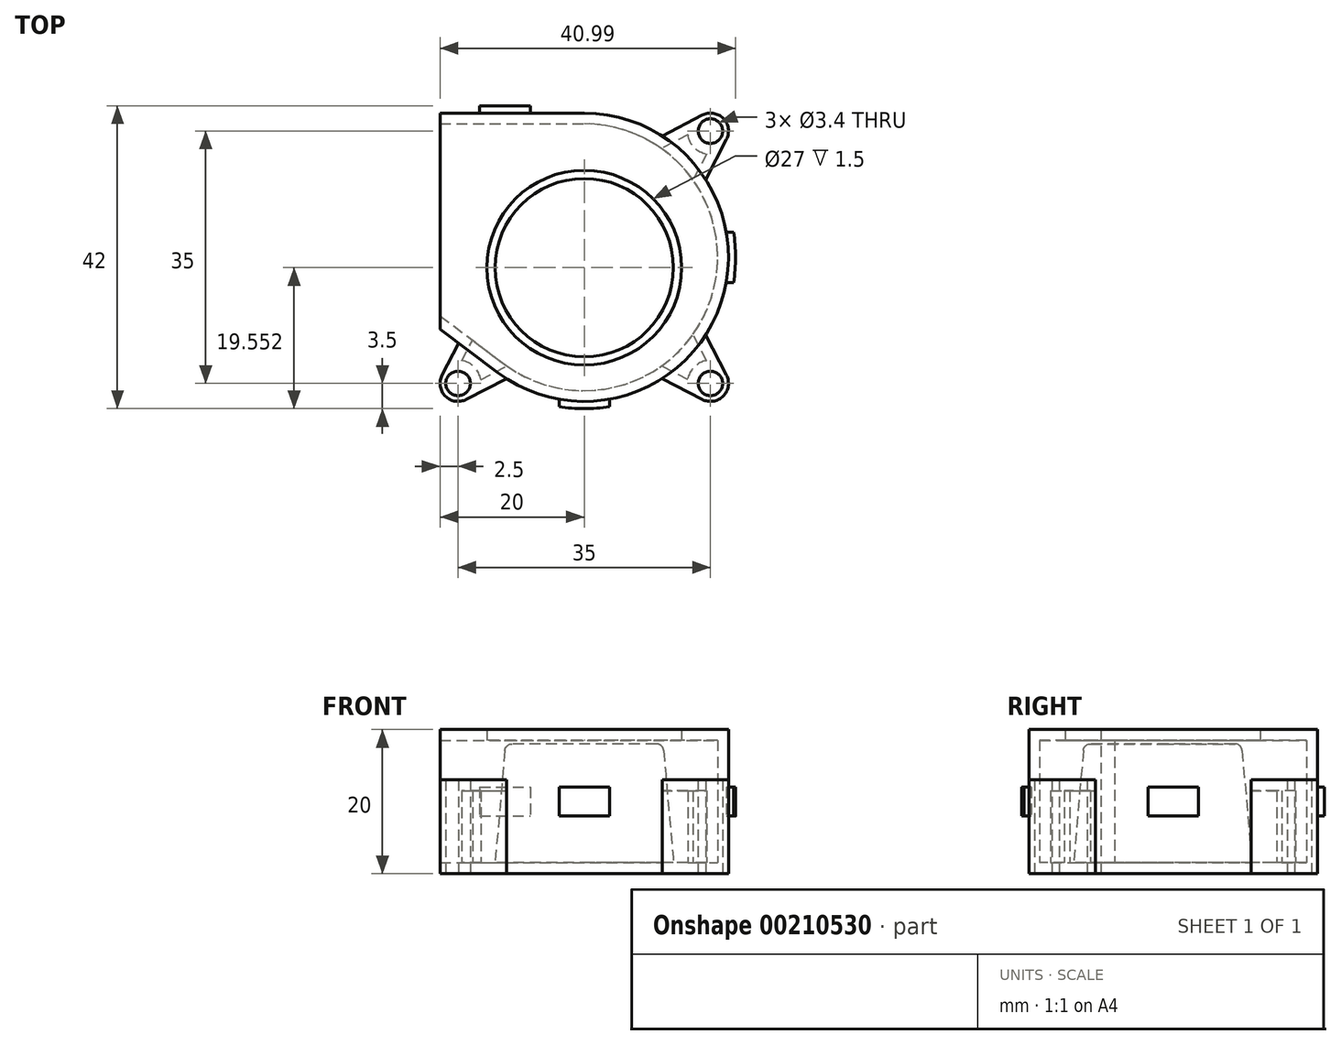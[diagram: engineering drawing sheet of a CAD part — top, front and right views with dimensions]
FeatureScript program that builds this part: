
annotation { "Feature Type Name" : "Feature", "Feature Type Description" : "" }
export const myFeature = defineFeature(function(context is Context, id is Id, definition is map)
    precondition{}
    {
        {
            var Q0;
            Q0=qCreatedBy(makeId("Top.planeOp"),FACE);
            var sketch = newSketch(context, id + "F0", { "sketchPlane" : qUnion([Q0])});
            skLineSegment(sketch, "E0.bottom", {"start": v(-20, 20) * mm, "end": v(0, 20) * mm});
            skPoint(sketch, "E0.middle", {"position": v(0, 0) * mm});
            skLineSegment(sketch, "E1", {"start": v(-20, -10) * mm, "end": v(-12, -16) * mm});
            skArc(sketch, "E2", {"start": v(-12, -16) * mm, "mid": v(18.97, -6.32) * mm, "end": v(0, 20) * mm});
            skLineSegment(sketch, "E3", {"start": v(16.35, 19.72) * mm, "end": v(10.8, 16.83) * mm});
            skLineSegment(sketch, "E4", {"start": v(19.72, 16.35) * mm, "end": v(16.83, 10.8) * mm});
            skArc(sketch, "E5", {"start": v(19.72, 16.35) * mm, "mid": v(19.27, 19.27) * mm, "end": v(16.35, 19.72) * mm});
            skLineSegment(sketch, "E6.bottom", {"start": v(17.5, -17.5) * mm, "end": v(-17.5, -17.5) * mm, "construction": true});
            skLineSegment(sketch, "E6.top", {"start": v(17.5, 17.5) * mm, "end": v(-17.5, 17.5) * mm, "construction": true});
            skLineSegment(sketch, "E6.left", {"start": v(17.5, -17.5) * mm, "end": v(17.5, 17.5) * mm, "construction": true});
            skLineSegment(sketch, "E6.right", {"start": v(-17.5, -17.5) * mm, "end": v(-17.5, 17.5) * mm, "construction": true});
            skCircle(sketch, "E7", {"center": v(17.5, 17.5) * mm, "radius": 1.7 * mm});
            skPoint(sketch, "E8", {"position": v(20, 0) * mm});
            skPoint(sketch, "E8.positionSnap0", {"position": v(17.5, 0) * mm});
            skPoint(sketch, "E9", {"position": v(0, -20) * mm});
            skLineSegment(sketch, "E10", {"start": v(-20, 20) * mm, "end": v(-20, -10) * mm});
            skCircle(sketch, "E11.1.0", {"center": v(17.5, -17.5) * mm, "radius": 1.7 * mm});
            skLineSegment(sketch, "E11.1.1", {"start": v(16.35, -19.72) * mm, "end": v(10.8, -16.83) * mm});
            skLineSegment(sketch, "E11.1.2", {"start": v(19.72, -16.35) * mm, "end": v(16.83, -10.8) * mm});
            skArc(sketch, "E11.1.3", {"start": v(16.35, -19.72) * mm, "mid": v(19.27, -19.27) * mm, "end": v(19.72, -16.35) * mm});
            skCircle(sketch, "E11.2.0", {"center": v(-17.5, -17.5) * mm, "radius": 1.7 * mm});
            skLineSegment(sketch, "E11.2.1", {"start": v(-19.72, -16.35) * mm, "end": v(-16.83, -10.8) * mm});
            skLineSegment(sketch, "E11.2.2", {"start": v(-16.35, -19.72) * mm, "end": v(-10.8, -16.83) * mm});
            skArc(sketch, "E11.2.3", {"start": v(-19.72, -16.35) * mm, "mid": v(-19.27, -19.27) * mm, "end": v(-16.35, -19.72) * mm});
            skLineSegment(sketch, "E11.anchor1", {"start": v(0, 0) * mm, "end": v(16.83, 10.8) * mm, "construction": true});
            skLineSegment(sketch, "E11.anchor2", {"start": v(0, 0) * mm, "end": v(-16.83, -10.8) * mm, "construction": true});
            skLineSegment(sketch, "E12", {"start": v(-3.5, -20.7) * mm, "end": v(-3.5, -19.7) * mm});
            skLineSegment(sketch, "E13", {"start": v(3.5, -20.7) * mm, "end": v(3.5, -19.7) * mm});
            skArc(sketch, "E14.trimOffspring", {"start": v(-3.5, -20.7) * mm, "mid": v(0, -21) * mm, "end": v(3.5, -20.7) * mm});
            skArc(sketch, "E15.trimOffspring", {"start": v(20.7, -3.5) * mm, "mid": v(20.99, 0) * mm, "end": v(20.7, 3.5) * mm});
            skLineSegment(sketch, "E16", {"start": v(19.7, -3.5) * mm, "end": v(20.7, -3.5) * mm});
            skLineSegment(sketch, "E17", {"start": v(19.7, 3.5) * mm, "end": v(20.7, 3.5) * mm});
            skSolve(sketch);
        }
        {
            var Q0;
            {var subQ6=sQuery(id+"F0.wireOp",EDGE,"E0.bottom");Q0=makeQuery(id+"F0.imprint","IMPRINT",FACE,{"disambiguationData":[TD([[makeQuery(id+"F0.imprint","IMPRINT",EDGE,{"derivedFrom":subQ6}),-1.0]])]});}
            extrude(context, id + "F1", {"entities" : qUnion([Q0]), "depth" : 20 * mm});
        }
        {
            var Q0;
            Q0=makeQuery(id+"F0.imprint","IMPRINT",FACE,{"disambiguationData":[TD([[makeQuery(id+"F0.imprint","IMPRINT",EDGE,{"derivedFrom":sQuery(id+"F0.wireOp",EDGE,"E11.2.0")}),-1.0]])]});
            var Q1;
            Q1=makeQuery(id+"F0.imprint","IMPRINT",FACE,{"disambiguationData":[TD([[makeQuery(id+"F0.imprint","IMPRINT",EDGE,{"derivedFrom":sQuery(id+"F0.wireOp",EDGE,"E11.1.0")}),-1.0]])]});
            var Q2;
            {var subQ1=sQuery(id+"F0.wireOp",EDGE,"E3");Q2=makeQuery(id+"F0.imprint","IMPRINT",FACE,{"disambiguationData":[TD([[makeQuery(id+"F0.imprint","IMPRINT",EDGE,{"derivedFrom":subQ1}),1.0]])]});}
            extrude(context, id + "F2", {"entities" : qUnion([Q0, Q1, Q2]), "operationType" : NewBodyOperationType.ADD, "depth" : 13 * mm});
        }
        {
            var Q0;
            Q0=makeQuery(id+"F1.opExtrude","SWEPT_FACE",FACE,{"disambiguationData":[OSD([sQuery(id+"F0.wireOp",EDGE,"E10")])]});
            shell(context, id + "F3", {"entities" : qUnion([Q0]), "thickness" : 1.5 * mm});
        }
        {
            var Q0;
            Q0=qCreatedBy(makeId("Top.planeOp"),FACE);
            var sketch = newSketch(context, id + "F4", { "sketchPlane" : qUnion([Q0])});
            skCircle(sketch, "E18", {"center": v(0, -1.45) * mm, "radius": 13.5 * mm});
            skCircle(sketch, "E19", {"center": v(0, -1.45) * mm, "radius": 12.5 * mm});
            skSolve(sketch);
        }
        {
            var Q0;
            Q0=makeQuery(id+"F4.imprint","IMPRINT",FACE,{"disambiguationData":[TD([[makeQuery(id+"F4.imprint","IMPRINT",EDGE,{"derivedFrom":sQuery(id+"F4.wireOp",EDGE,"E18")}),1.0]])]});
            var Q1;
            Q1=makeQuery(id+"F4.imprint","IMPRINT",FACE,{"disambiguationData":[TD([[makeQuery(id+"F4.imprint","IMPRINT",EDGE,{"derivedFrom":sQuery(id+"F4.wireOp",EDGE,"E19")}),1.0]])]});
            extrude(context, id + "F5", {"entities" : qUnion([Q0, Q1]), "operationType" : NewBodyOperationType.REMOVE, "depth" : 25 * mm, "hasSecondDirection" : true, "secondDirectionOppositeDirection" : false, "secondDirectionDepth" : 5 * mm});
        }
        {
            var Q0;
            Q0=makeQuery(id+"F4.imprint","IMPRINT",FACE,{"disambiguationData":[TD([[makeQuery(id+"F4.imprint","IMPRINT",EDGE,{"derivedFrom":sQuery(id+"F4.wireOp",EDGE,"E19")}),1.0]])]});
            extrude(context, id + "F6", {"entities" : qUnion([Q0]), "operationType" : NewBodyOperationType.ADD, "depth" : 18 * mm, "hasDraft" : true, "draftAngle" : 5 * degree, "draftPullDirection" : true});
        }
        {
            var Q0;
            Q0=makeQuery(id+"F6.opExtrude","CAP_FACE",FACE,{"disambiguationData":[OSD([sQuery(id+"F4.wireOp",EDGE,"E19")])],"isStart":false});
            fillet(context, id + "F7", {"entities" : qUnion([Q0]), "radius" : 1 * mm, "tangentPropagation" : true, "allowEdgeOverflow" : false});
        }
        {
            var Q0;
            Q0=makeQuery(id+"F1.opExtrude","SWEPT_FACE",FACE,{"disambiguationData":[OSD([sQuery(id+"F0.wireOp",EDGE,"E0.bottom")])]});
            var sketch = newSketch(context, id + "F8", { "sketchPlane" : qUnion([Q0])});
            skLineSegment(sketch, "E20.bottom", {"start": v(14.5, 12) * mm, "end": v(7.5, 12) * mm});
            skLineSegment(sketch, "E20.top", {"start": v(14.5, 8) * mm, "end": v(7.5, 8) * mm});
            skLineSegment(sketch, "E20.left", {"start": v(14.5, 12) * mm, "end": v(14.5, 8) * mm});
            skLineSegment(sketch, "E20.right", {"start": v(7.5, 12) * mm, "end": v(7.5, 8) * mm});
            skPoint(sketch, "E21", {"position": v(7.5, 10) * mm});
            skPoint(sketch, "E22", {"position": v(0, 10) * mm});
            skSolve(sketch);
        }
        {
            var Q0;
            Q0=qSketchRegion(id+"F8",true);
            extrude(context, id + "F9", {"entities" : qUnion([Q0]), "operationType" : NewBodyOperationType.ADD, "depth" : 1 * mm});
        }
        {
            var Q0;
            Q0=makeQuery(id+"F0.imprint","IMPRINT",FACE,{"disambiguationData":[TD([[makeQuery(id+"F0.imprint","IMPRINT",EDGE,{"derivedFrom":sQuery(id+"F0.wireOp",EDGE,"E15.trimOffspring")}),1.0]])]});
            var Q1;
            {var subQ0=sQuery(id+"F0.wireOp",EDGE,"E12");Q1=makeQuery(id+"F0.imprint","IMPRINT",FACE,{"disambiguationData":[TD([[makeQuery(id+"F0.imprint","IMPRINT",EDGE,{"derivedFrom":subQ0}),-1.0]])]});}
            extrude(context, id + "F10", {"entities" : qUnion([Q0, Q1]), "operationType" : NewBodyOperationType.ADD, "depth" : 12 * mm, "hasSecondDirection" : true, "secondDirectionOppositeDirection" : false, "secondDirectionDepth" : 8 * mm});
        }
    });
